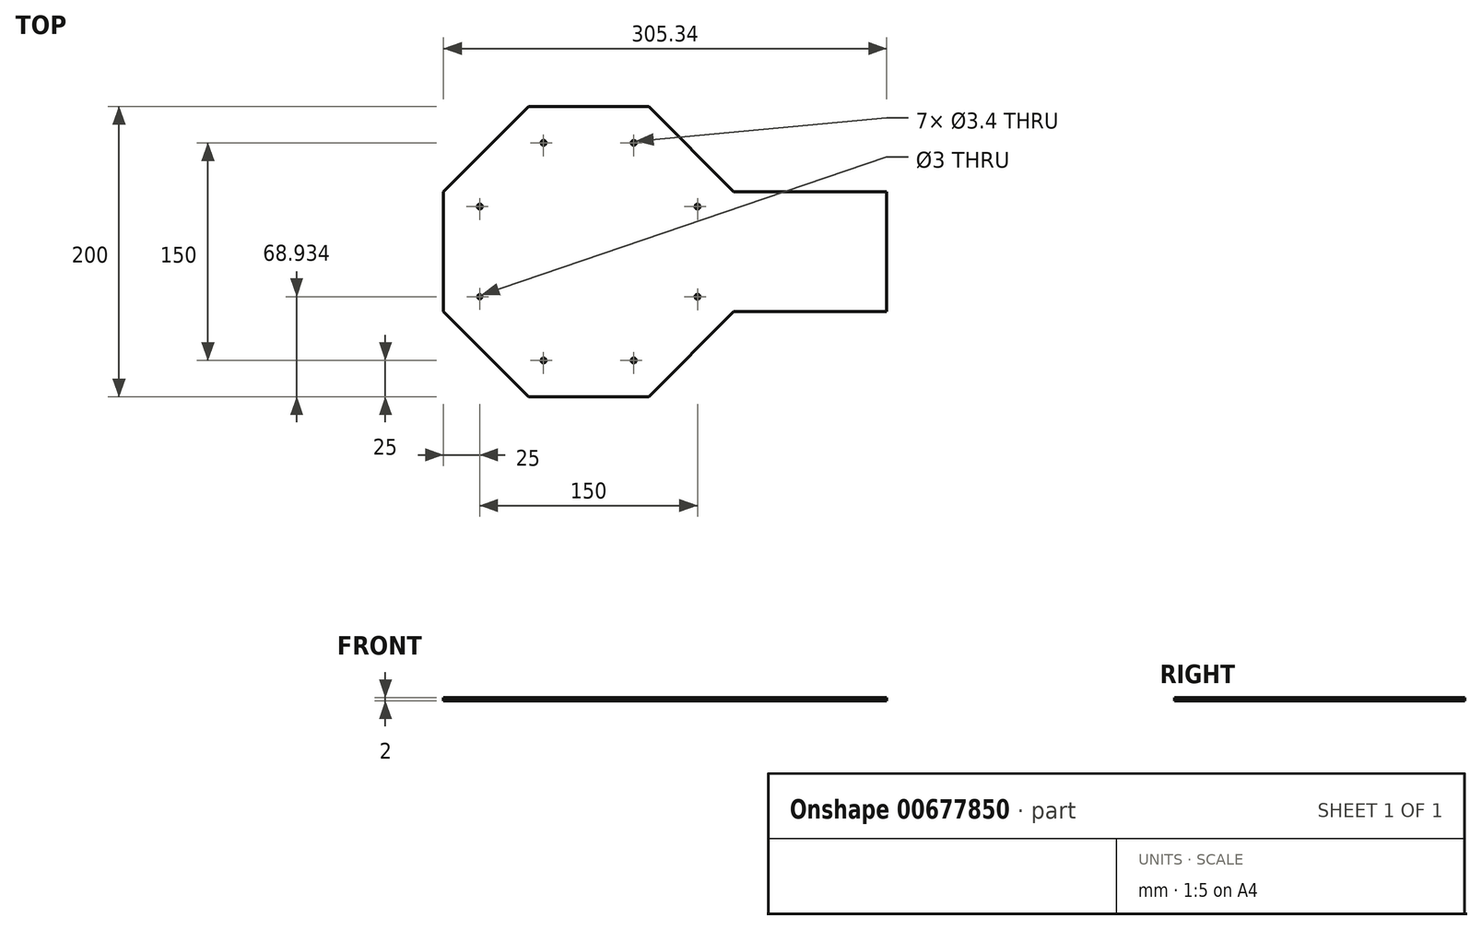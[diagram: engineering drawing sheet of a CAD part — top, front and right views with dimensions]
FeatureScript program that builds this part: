
annotation { "Feature Type Name" : "Feature", "Feature Type Description" : "" }
export const myFeature = defineFeature(function(context is Context, id is Id, definition is map)
    precondition{}
    {
        {
            var Q0;
            Q0=qCreatedBy(makeId("Top.planeOp"),FACE);
            var sketch = newSketch(context, id + "F0", { "sketchPlane" : qUnion([Q0])});
            skLineSegment(sketch, "E0.0", {"start": v(-41.42, 100) * mm, "end": v(41.42, 100) * mm});
            skLineSegment(sketch, "E0.1", {"start": v(41.42, 100) * mm, "end": v(100, 41.42) * mm});
            skLineSegment(sketch, "E0.3", {"start": v(100, -41.42) * mm, "end": v(41.42, -100) * mm});
            skLineSegment(sketch, "E0.4", {"start": v(41.42, -100) * mm, "end": v(-41.42, -100) * mm});
            skLineSegment(sketch, "E0.5", {"start": v(-41.42, -100) * mm, "end": v(-100, -41.42) * mm});
            skLineSegment(sketch, "E0.6", {"start": v(-100, -41.42) * mm, "end": v(-100, 41.42) * mm});
            skLineSegment(sketch, "E0.7", {"start": v(-100, 41.42) * mm, "end": v(-41.42, 100) * mm});
            skLineSegment(sketch, "E1.bottom", {"start": v(100, 41.42) * mm, "end": v(205.34, 41.42) * mm});
            skLineSegment(sketch, "E1.top", {"start": v(100, -41.42) * mm, "end": v(205.34, -41.42) * mm});
            skLineSegment(sketch, "E1.right", {"start": v(205.34, 41.42) * mm, "end": v(205.34, -41.42) * mm});
            skCircle(sketch, "E2", {"center": v(-31.07, 75) * mm, "radius": 1.7 * mm});
            skCircle(sketch, "E3", {"center": v(31.07, 75) * mm, "radius": 1.7 * mm});
            skCircle(sketch, "E4", {"center": v(75, 31.07) * mm, "radius": 1.7 * mm});
            skCircle(sketch, "E5", {"center": v(75, -31.07) * mm, "radius": 1.7 * mm});
            skCircle(sketch, "E6", {"center": v(31.07, -75) * mm, "radius": 1.7 * mm});
            skCircle(sketch, "E7", {"center": v(-31.07, -75) * mm, "radius": 1.7 * mm});
            skCircle(sketch, "E8", {"center": v(-75, -31.07) * mm, "radius": 1.5 * mm});
            skCircle(sketch, "E9", {"center": v(-75, 31.07) * mm, "radius": 1.7 * mm});
            skPoint(sketch, "E10.0.midPoint", {"position": v(0, 100) * mm});
            skSolve(sketch);
        }
        {
            var Q0;
            Q0=makeQuery(id+"F0.imprint","IMPRINT",FACE,{"disambiguationData":[TD([[makeQuery(id+"F0.imprint","IMPRINT",EDGE,{"derivedFrom":sQuery(id+"F0.wireOp",EDGE,"E0.0")}),-1.0]])]});
            extrude(context, id + "F1", {"entities" : qUnion([Q0]), "depth" : 2 * mm, "offsetDistance" : 25 * mm});
        }
    });
